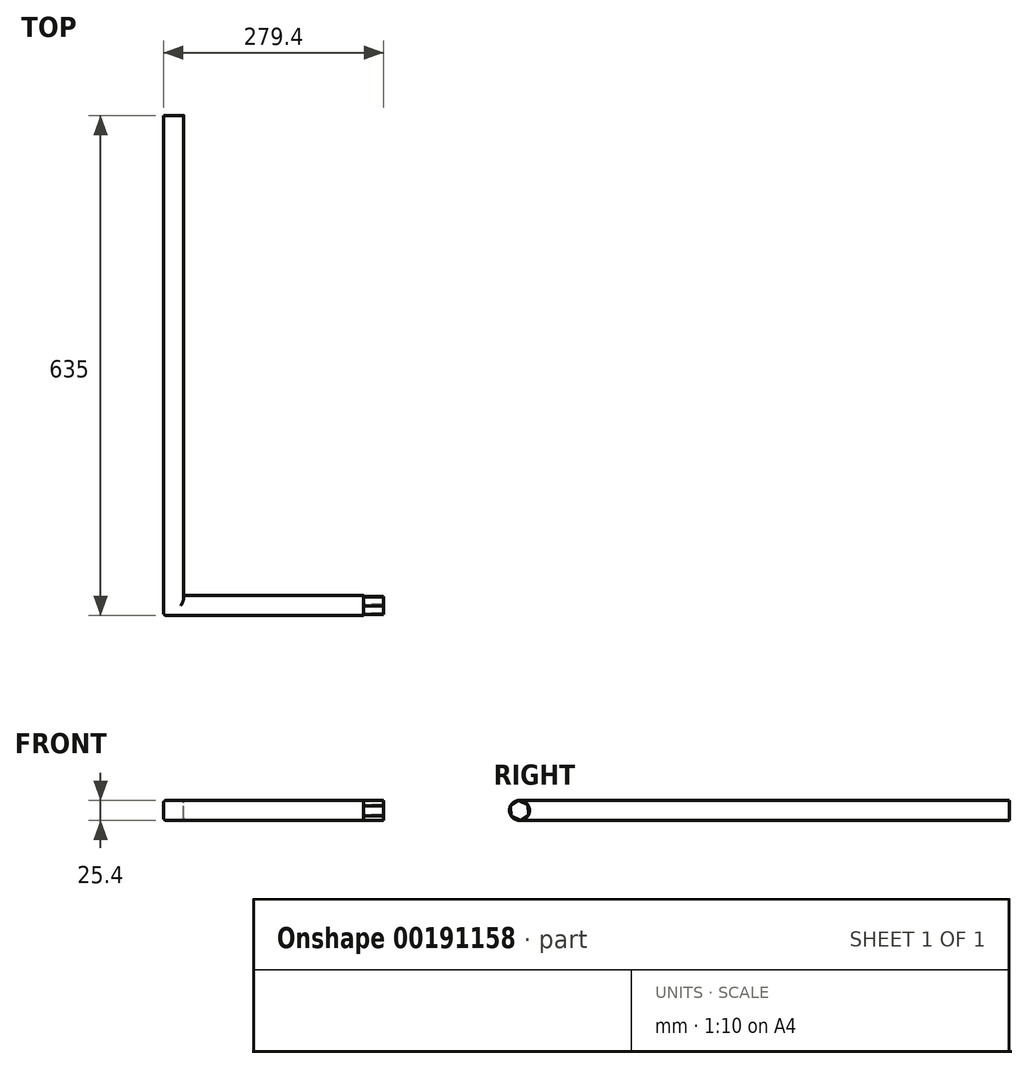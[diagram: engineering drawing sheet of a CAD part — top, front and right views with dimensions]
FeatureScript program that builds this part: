
annotation { "Feature Type Name" : "Feature", "Feature Type Description" : "" }
export const myFeature = defineFeature(function(context is Context, id is Id, definition is map)
    precondition{}
    {
        {
            var Q0;
            Q0=qCreatedBy(makeId("Front.planeOp"),FACE);
            var sketch = newSketch(context, id + "F0", { "sketchPlane" : qUnion([Q0])});
            skLineSegment(sketch, "E0.bottom", {"start": v(-12.7, -12.7) * mm, "end": v(12.7, -12.7) * mm});
            skLineSegment(sketch, "E0.top", {"start": v(-12.7, 12.7) * mm, "end": v(12.7, 12.7) * mm});
            skLineSegment(sketch, "E0.left", {"start": v(-12.7, -12.7) * mm, "end": v(-12.7, 12.7) * mm});
            skLineSegment(sketch, "E0.right", {"start": v(12.7, -12.7) * mm, "end": v(12.7, 12.7) * mm});
            skPoint(sketch, "E0.middle", {"position": v(0, 0) * mm});
            skSolve(sketch);
        }
        {
            var Q0;
            Q0 = qSketchRegion(id + "F0", true);
            extrude(context, id + "F1", {"entities" : qUnion([Q0]), "depth" : 635 * mm});
        }
        {
            var Q0;
            Q0=makeQuery(id+"F1.opExtrude","SWEPT_FACE",FACE,{"disambiguationData":[OSD([sQuery(id+"F0.wireOp",EDGE,"E0.right")])]});
            var sketch = newSketch(context, id + "F2", { "sketchPlane" : qUnion([Q0])});
            skPoint(sketch, "E1.endSnap0", {"position": v(-635, 0) * mm});
            skCircle(sketch, "E2", {"center": v(-622.3, 0) * mm, "radius": 12.7 * mm});
            skSolve(sketch);
        }
        {
            var Q0;
            Q0 = qSketchRegion(id + "F2", true);
            extrude(context, id + "F3", {"entities" : qUnion([Q0]), "operationType" : NewBodyOperationType.ADD, "depth" : 228.6 * mm});
        }
        {
            var Q0;
            Q0=makeQuery(id+"F1.opExtrude","CAP_EDGE",EDGE,{"disambiguationData":[OSD([sQuery(id+"F0.wireOp",EDGE,"E0.top")])],"isStart":false});
            fillet(context, id + "F4", {"entities" : qUnion([Q0]), "radius" : 12.7 * mm, "tangentPropagation" : true, "allowEdgeOverflow" : false});
        }
        {
            var Q0;
            Q0=makeQuery(id+"F1.opExtrude","CAP_EDGE",EDGE,{"disambiguationData":[OSD([sQuery(id+"F0.wireOp",EDGE,"E0.bottom")])],"isStart":false});
            fillet(context, id + "F5", {"entities" : qUnion([Q0]), "radius" : 12.7 * mm, "tangentPropagation" : true, "allowEdgeOverflow" : false});
        }
        {
            var Q0;
            Q0=makeQuery(id+"F3.opExtrude","CAP_FACE",FACE,{"disambiguationData":[OSD([sQuery(id+"F2.wireOp",EDGE,"E2")])],"isStart":false});
            var sketch = newSketch(context, id + "F6", { "sketchPlane" : qUnion([Q0])});
            skCircle(sketch, "E3.cCircle", {"center": v(-622.3, 0) * mm, "radius": 12.7 * mm, "construction": true});
            skLineSegment(sketch, "E3.0", {"start": v(-623.28, 12.66) * mm, "end": v(-611.82, 7.18) * mm});
            skLineSegment(sketch, "E3.1", {"start": v(-611.82, 7.18) * mm, "end": v(-610.85, -5.49) * mm});
            skLineSegment(sketch, "E3.2", {"start": v(-610.85, -5.49) * mm, "end": v(-621.32, -12.66) * mm});
            skLineSegment(sketch, "E3.3", {"start": v(-621.32, -12.66) * mm, "end": v(-632.78, -7.18) * mm});
            skLineSegment(sketch, "E3.4", {"start": v(-632.78, -7.18) * mm, "end": v(-633.75, 5.49) * mm});
            skLineSegment(sketch, "E3.5", {"start": v(-633.75, 5.49) * mm, "end": v(-623.28, 12.66) * mm});
            skSolve(sketch);
        }
        {
            var Q0;
            Q0 = qSketchRegion(id + "F6", true);
            extrude(context, id + "F7", {"entities" : qUnion([Q0]), "operationType" : NewBodyOperationType.ADD, "depth" : 25.4 * mm});
        }
        {
            var Q0;
            {var subQ0=sQuery(id+"F0.wireOp",EDGE,"E0.right");var subQ1=sQuery(id+"F0.wireOp",EDGE,"E0.top");Q0=makeQuery(id+"F3.boolean.opBoolean","SPLIT",EDGE,{"disambiguationData":[TD([makeQuery(id+"F1.opExtrude","CAP_FACE",FACE,{"disambiguationData":[OSD([sQuery(id+"F0.wireOp",EDGE,"E0.bottom"),subQ1,sQuery(id+"F0.wireOp",EDGE,"E0.left"),subQ0])],"isStart":true})])],"derivedFrom":makeQuery(id+"F1.opExtrude","SWEPT_EDGE",EDGE,{"disambiguationData":[OSD([subQ1,subQ0])]})});}
            var Q1;
            Q1=makeQuery(id+"F1.opExtrude","SWEPT_EDGE",EDGE,{"disambiguationData":[OSD([sQuery(id+"F0.wireOp",EDGE,"E0.top"),sQuery(id+"F0.wireOp",EDGE,"E0.left")])]});
            var Q2;
            {var subQ0=sQuery(id+"F0.wireOp",EDGE,"E0.bottom");var subQ1=sQuery(id+"F0.wireOp",EDGE,"E0.right");Q2=makeQuery(id+"F3.boolean.opBoolean","SPLIT",EDGE,{"disambiguationData":[TD([makeQuery(id+"F1.opExtrude","CAP_FACE",FACE,{"disambiguationData":[OSD([subQ0,sQuery(id+"F0.wireOp",EDGE,"E0.top"),sQuery(id+"F0.wireOp",EDGE,"E0.left"),subQ1])],"isStart":true})])],"derivedFrom":makeQuery(id+"F1.opExtrude","SWEPT_EDGE",EDGE,{"disambiguationData":[OSD([subQ0,subQ1])]})});}
            var Q3;
            Q3=makeQuery(id+"F1.opExtrude","SWEPT_EDGE",EDGE,{"disambiguationData":[OSD([sQuery(id+"F0.wireOp",EDGE,"E0.bottom"),sQuery(id+"F0.wireOp",EDGE,"E0.left")])]});
            fillet(context, id + "F8", {"entities" : qUnion([Q0, Q1, Q2, Q3]), "radius" : 3.17 * mm, "tangentPropagation" : true, "allowEdgeOverflow" : false});
        }
    });
